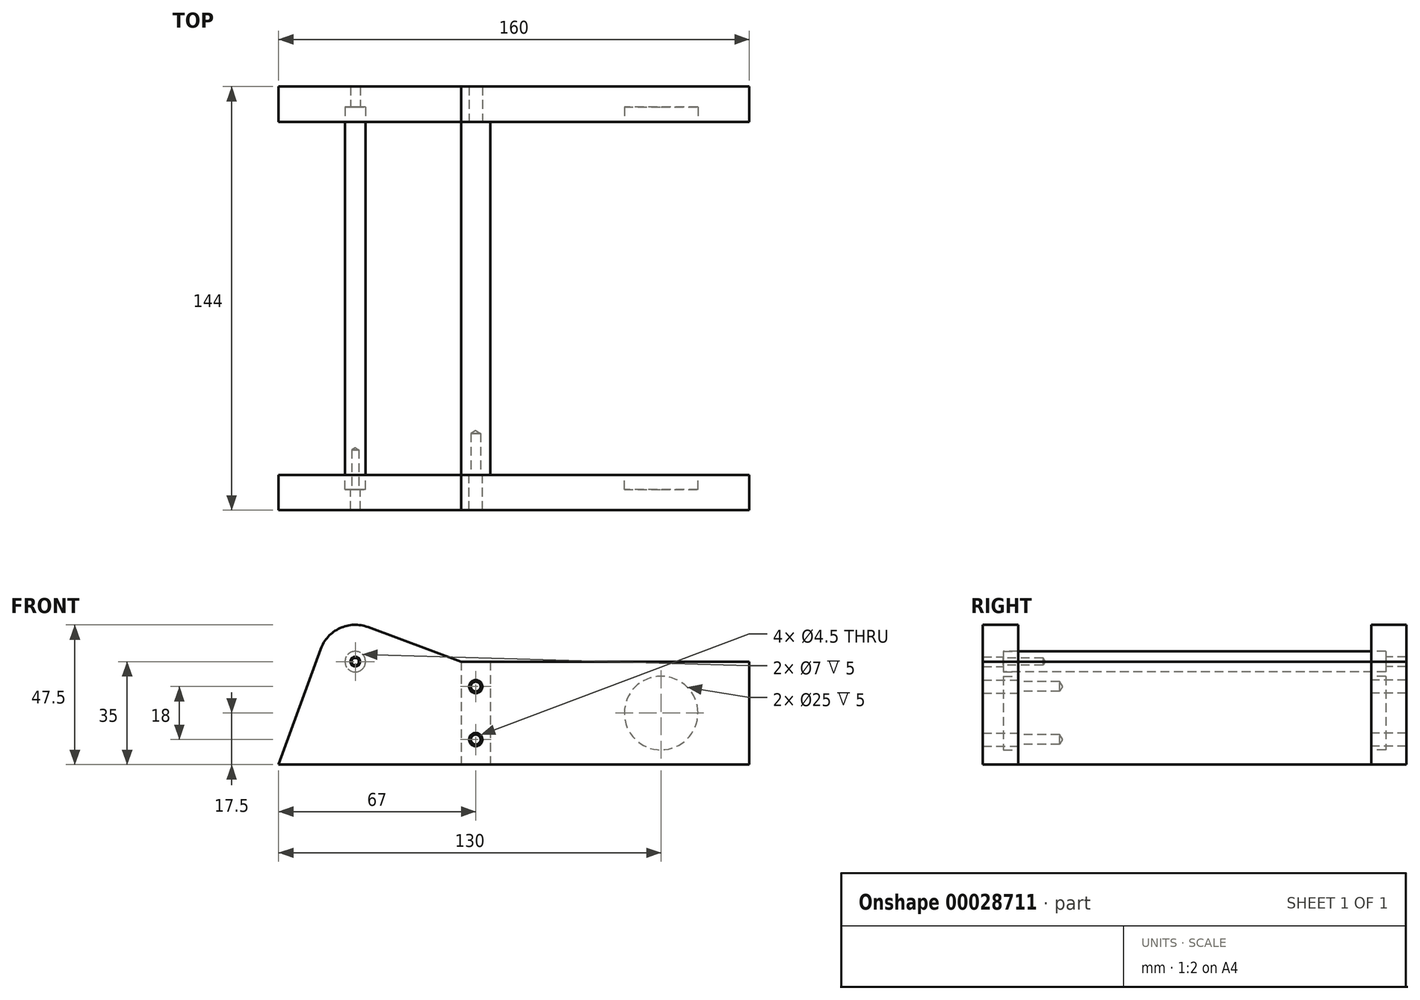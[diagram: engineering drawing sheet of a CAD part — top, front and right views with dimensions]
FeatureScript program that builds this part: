
annotation { "Feature Type Name" : "Feature", "Feature Type Description" : "" }
export const myFeature = defineFeature(function(context is Context, id is Id, definition is map)
    precondition{}
    {
        {
            var Q0;
            Q0=qCreatedBy(makeId("Front.planeOp"),FACE);
            var sketch = newSketch(context, id + "F0", { "sketchPlane" : qUnion([Q0])});
            skCircle(sketch, "E0", {"center": v(26.04, 35) * mm, "radius": 40 * mm, "construction": true});
            skArc(sketch, "E1", {"start": v(30.39, 46.72) * mm, "mid": v(20.8, 46.34) * mm, "end": v(14.3, 39.28) * mm});
            skLineSegment(sketch, "E2", {"start": v(0, 0) * mm, "end": v(14.3, 39.28) * mm});
            skLineSegment(sketch, "E3", {"start": v(30.39, 46.72) * mm, "end": v(62, 35) * mm});
            skLineSegment(sketch, "E4", {"start": v(62, 35) * mm, "end": v(160, 35) * mm});
            skLineSegment(sketch, "E5", {"start": v(0, 0) * mm, "end": v(160, 0) * mm});
            skLineSegment(sketch, "E6", {"start": v(160, 0) * mm, "end": v(160, 35) * mm});
            skCircle(sketch, "E7", {"center": v(26.04, 35) * mm, "radius": 1.65 * mm});
            skSolve(sketch);
        }
        {
            var Q0;
            Q0 = qSketchRegion(id + "F0", true);
            extrude(context, id + "F1", {"entities" : qUnion([Q0]), "depth" : 12 * mm, "offsetDistance" : 25 * mm});
        }
        {
            var Q0;
            Q0=makeQuery(id+"F1.opExtrude","CAP_FACE",FACE,{"disambiguationData":[OSD([sQuery(id+"F0.wireOp",EDGE,"E1"),sQuery(id+"F0.wireOp",EDGE,"E2"),sQuery(id+"F0.wireOp",EDGE,"E3"),sQuery(id+"F0.wireOp",EDGE,"E4"),sQuery(id+"F0.wireOp",EDGE,"E5"),sQuery(id+"F0.wireOp",EDGE,"E6"),sQuery(id+"F0.wireOp",EDGE,"E7")])],"isStart":true});
            var sketch = newSketch(context, id + "F2", { "sketchPlane" : qUnion([Q0])});
            skCircle(sketch, "E8", {"center": v(-26.04, 35) * mm, "radius": 3.5 * mm});
            skSolve(sketch);
        }
        {
            var Q0;
            Q0 = qSketchRegion(id + "F2", true);
            extrude(context, id + "F3", {"entities" : qUnion([Q0]), "operationType" : NewBodyOperationType.REMOVE, "oppositeDirection" : true, "depth" : 5 * mm, "offsetDistance" : 25 * mm});
        }
        {
            var Q0;
            Q0=makeQuery(id+"F1.opExtrude","CAP_FACE",FACE,{"disambiguationData":[OSD([sQuery(id+"F0.wireOp",EDGE,"E1"),sQuery(id+"F0.wireOp",EDGE,"E2"),sQuery(id+"F0.wireOp",EDGE,"E3"),sQuery(id+"F0.wireOp",EDGE,"E4"),sQuery(id+"F0.wireOp",EDGE,"E5"),sQuery(id+"F0.wireOp",EDGE,"E6"),sQuery(id+"F0.wireOp",EDGE,"E7")])],"isStart":true});
            var sketch = newSketch(context, id + "F4", { "sketchPlane" : qUnion([Q0])});
            skLineSegment(sketch, "E9.bottom", {"start": v(-62, 35) * mm, "end": v(-72, 35) * mm});
            skLineSegment(sketch, "E9.top", {"start": v(-62, 0) * mm, "end": v(-72, 0) * mm});
            skLineSegment(sketch, "E9.left", {"start": v(-62, 35) * mm, "end": v(-62, 0) * mm});
            skLineSegment(sketch, "E9.right", {"start": v(-72, 35) * mm, "end": v(-72, 0) * mm});
            skLineSegment(sketch, "E10", {"start": v(-67, 35) * mm, "end": v(-67, 0) * mm, "construction": true});
            skLineSegment(sketch, "E11", {"start": v(-67, 17.5) * mm, "end": v(-83.22, 17.5) * mm, "construction": true});
            skPoint(sketch, "E12", {"position": v(-67, 26.5) * mm});
            skPoint(sketch, "E13.MirrorP", {"position": v(-67, 8.5) * mm});
            skSolve(sketch);
        }
        {
            var Q0;
            Q0 = qSketchRegion(id + "F4", true);
            extrude(context, id + "F5", {"entities" : qUnion([Q0]), "depth" : 120 * mm, "offsetDistance" : 25 * mm});
        }
        {
            var Q0;
            Q0=sQuery(id+"F4.wireOp",VERTEX,"E12");
            var Q1;
            Q1=sQuery(id+"F4.wireOp",VERTEX,"E13.MirrorP");
            var Q2;
            Q2=makeQuery(id+"F5.opExtrude","SWEPT_BODY",BODY,{"disambiguationData":[OSD([sQuery(id+"F4.wireOp",EDGE,"E9.bottom"),sQuery(id+"F4.wireOp",EDGE,"E9.top"),sQuery(id+"F4.wireOp",EDGE,"E9.left"),sQuery(id+"F4.wireOp",EDGE,"E9.right")])]});
            hole(context, id + "F6", {"style" : HoleStyle.SIMPLE, "endStyle" : HoleEndStyle.BLIND, "oppositeDirection" : true, "standardTappedOrClearance" : lookupTablePath({ "standard" : "ISO", "engagement" : "75%", "pitch" : "0.7 mm", "size" : "M4", "type" : "Tapped" }), "standardBlindInLast" : lookupTablePath({ "standard" : "ISO", "fit" : "Normal", "engagement" : "75%", "pitch" : "0.7 mm", "size" : "M4", "type" : "Clearance & tapped" }), "holeDiameter" : 3.3 * mm, "majorDiameter" : 4 * mm, "showTappedDepth" : true, "holeDepth" : 14.1 * mm, "isTappedThrough" : true, "tappedDepth" : 12 * mm, "tapClearance" : 3, "locations" : qUnion([Q0, Q1]), "scope" : qUnion([Q2])});
        }
        {
            var Q0;
            Q0=sQuery(id+"F4.wireOp",VERTEX,"E12");
            var Q1;
            Q1=sQuery(id+"F4.wireOp",VERTEX,"E13.MirrorP");
            var Q2;
            Q2=makeQuery(id+"F1.opExtrude","SWEPT_BODY",BODY,{"disambiguationData":[OSD([sQuery(id+"F0.wireOp",EDGE,"E1"),sQuery(id+"F0.wireOp",EDGE,"E2"),sQuery(id+"F0.wireOp",EDGE,"E3"),sQuery(id+"F0.wireOp",EDGE,"E4"),sQuery(id+"F0.wireOp",EDGE,"E5"),sQuery(id+"F0.wireOp",EDGE,"E6"),sQuery(id+"F0.wireOp",EDGE,"E7")])]});
            hole(context, id + "F7", {"style" : HoleStyle.SIMPLE, "endStyle" : HoleEndStyle.BLIND, "standardTappedOrClearance" : lookupTablePath({ "fit" : "Normal", "standard" : "ISO", "size" : "M4", "type" : "Clearance" }), "standardBlindInLast" : lookupTablePath({ "fit" : "Normal", "standard" : "ISO", "engagement" : "75%", "pitch" : "0.7 mm", "size" : "M4", "type" : "Clearance & tapped" }), "holeDiameter" : 4.5 * mm, "majorDiameter" : 4 * mm, "holeDepth" : 14.1 * mm, "isTappedThrough" : true, "tappedDepth" : 12 * mm, "tapClearance" : 3, "locations" : qUnion([Q0, Q1]), "scope" : qUnion([Q2])});
        }
        {
            var Q0;
            Q0=makeQuery(id+"F5.opExtrude","CAP_FACE",FACE,{"disambiguationData":[OSD([sQuery(id+"F4.wireOp",EDGE,"E9.bottom"),sQuery(id+"F4.wireOp",EDGE,"E9.top"),sQuery(id+"F4.wireOp",EDGE,"E9.left"),sQuery(id+"F4.wireOp",EDGE,"E9.right")])],"isStart":true});
            var Q1;
            Q1=makeQuery(id+"F5.opExtrude","CAP_FACE",FACE,{"disambiguationData":[OSD([sQuery(id+"F4.wireOp",EDGE,"E9.bottom"),sQuery(id+"F4.wireOp",EDGE,"E9.top"),sQuery(id+"F4.wireOp",EDGE,"E9.left"),sQuery(id+"F4.wireOp",EDGE,"E9.right")])],"isStart":false});
            cPlane(context, id + "F8", {"entities" : qUnion([Q0, Q1]), "cplaneType" : CPlaneType.MID_PLANE, "offset" : 25 * mm, "width" : 150 * mm, "height" : 150 * mm});
        }
        {
            var Q0;
            Q0=makeQuery(id+"F1.opExtrude","CAP_FACE",FACE,{"disambiguationData":[OSD([sQuery(id+"F0.wireOp",EDGE,"E1"),sQuery(id+"F0.wireOp",EDGE,"E2"),sQuery(id+"F0.wireOp",EDGE,"E3"),sQuery(id+"F0.wireOp",EDGE,"E4"),sQuery(id+"F0.wireOp",EDGE,"E5"),sQuery(id+"F0.wireOp",EDGE,"E6"),sQuery(id+"F0.wireOp",EDGE,"E7")])],"isStart":true});
            var sketch = newSketch(context, id + "F9", { "sketchPlane" : qUnion([Q0])});
            skCircle(sketch, "E14", {"center": v(-130, 17.5) * mm, "radius": 12.5 * mm});
            skLineSegment(sketch, "E15", {"start": v(-130, 17.5) * mm, "end": v(-160, 17.5) * mm, "construction": true});
            skPoint(sketch, "E15.endSnap0", {"position": v(-160, 17.5) * mm});
            skSolve(sketch);
        }
        {
            var Q0;
            Q0 = qSketchRegion(id + "F9", true);
            extrude(context, id + "F10", {"entities" : qUnion([Q0]), "operationType" : NewBodyOperationType.REMOVE, "oppositeDirection" : true, "depth" : 5 * mm, "offsetDistance" : 25 * mm});
        }
        {
            var Q0;
            Q0=makeQuery(id+"F1.opExtrude","SWEPT_BODY",BODY,{"disambiguationData":[OSD([sQuery(id+"F0.wireOp",EDGE,"E1"),sQuery(id+"F0.wireOp",EDGE,"E2"),sQuery(id+"F0.wireOp",EDGE,"E3"),sQuery(id+"F0.wireOp",EDGE,"E4"),sQuery(id+"F0.wireOp",EDGE,"E5"),sQuery(id+"F0.wireOp",EDGE,"E6"),sQuery(id+"F0.wireOp",EDGE,"E7")])]});
            var Q1;
            Q1=qCreatedBy(id+"F8.planeOp",FACE);
            mirror(context, id + "F11", {"entities" : qUnion([Q0]), "mirrorPlane" : qUnion([Q1])});
        }
        {
            var Q0;
            Q0=makeQuery(id+"F3.boolean.opBoolean","COPY",FACE,{"derivedFrom":makeQuery(id+"F3.opExtrude","CAP_FACE",FACE,{"disambiguationData":[OSD([sQuery(id+"F2.wireOp",EDGE,"E8")])],"isStart":false})});
            var sketch = newSketch(context, id + "F12", { "sketchPlane" : qUnion([Q0])});
            skCircle(sketch, "E16.0", {"center": v(-26.04, 35) * mm, "radius": 3.5 * mm});
            skSolve(sketch);
        }
        {
            var Q0;
            Q0 = qSketchRegion(id + "F12", true);
            var Q1;
            Q1=makeQuery(id+"F11.opPattern","COPY",FACE,{"derivedFrom":makeQuery(id+"F3.boolean.opBoolean","COPY",FACE,{"derivedFrom":makeQuery(id+"F3.opExtrude","CAP_FACE",FACE,{"disambiguationData":[OSD([sQuery(id+"F2.wireOp",EDGE,"E8")])],"isStart":false})}),"instanceName":"1"});
            extrude(context, id + "F13", {"entities" : qUnion([Q0]), "endBound" : BoundingType.UP_TO_SURFACE, "depth" : 25 * mm, "endBoundEntityFace" : qUnion([Q1]), "offsetDistance" : 25 * mm});
        }
        {
            var Q0;
            Q0=makeQuery(id+"F13.opExtrude","CAP_FACE",FACE,{"disambiguationData":[OSD([sQuery(id+"F12.wireOp",EDGE,"E16.0")])],"isStart":true});
            var sketch = newSketch(context, id + "F14", { "sketchPlane" : qUnion([Q0])});
            skPoint(sketch, "E17", {"position": v(26.04, 35) * mm});
            skSolve(sketch);
        }
        {
            var Q0;
            Q0=sQuery(id+"F14.wireOp",VERTEX,"E17");
            var Q1;
            Q1=makeQuery(id+"F13.opExtrude","SWEPT_BODY",BODY,{"disambiguationData":[OSD([sQuery(id+"F12.wireOp",EDGE,"E16.0")])]});
            hole(context, id + "F15", {"style" : HoleStyle.SIMPLE, "endStyle" : HoleEndStyle.BLIND, "standardTappedOrClearance" : lookupTablePath({ "standard" : "ISO", "engagement" : "75%", "pitch" : "0.5 mm", "size" : "M3", "type" : "Tapped" }), "standardBlindInLast" : lookupTablePath({ "standard" : "ISO", "fit" : "Normal", "engagement" : "75%", "pitch" : "0.5 mm", "size" : "M3", "type" : "Clearance & tapped" }), "holeDiameter" : 2.5 * mm, "majorDiameter" : 3 * mm, "showTappedDepth" : true, "holeDepth" : 13.5 * mm, "isTappedThrough" : true, "tappedDepth" : 12 * mm, "tapClearance" : 3, "locations" : qUnion([Q0]), "scope" : qUnion([Q1])});
        }
    });
